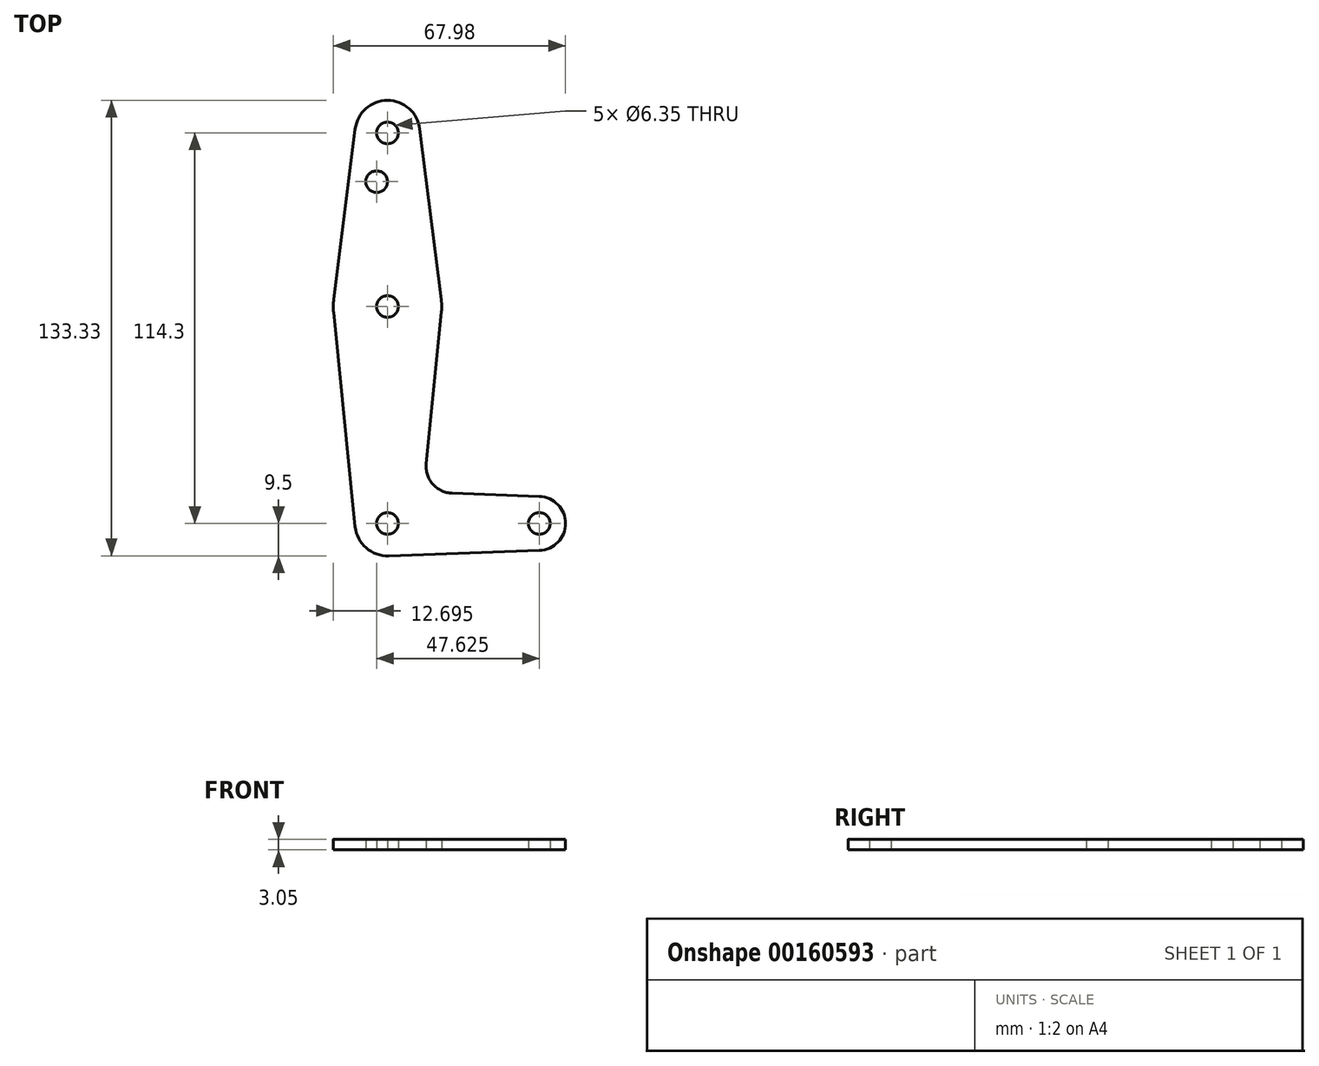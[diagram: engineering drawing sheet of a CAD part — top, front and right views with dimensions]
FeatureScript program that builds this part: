
annotation { "Feature Type Name" : "Feature", "Feature Type Description" : "" }
export const myFeature = defineFeature(function(context is Context, id is Id, definition is map)
    precondition{}
    {
        {
            var Q0;
            Q0=qCreatedBy(makeId("Top.planeOp"),FACE);
            var sketch = newSketch(context, id + "F0", { "sketchPlane" : qUnion([Q0])});
            skLineSegment(sketch, "E0", {"start": v(0, 0) * mm, "end": v(44.45, 0) * mm, "construction": true});
            skLineSegment(sketch, "E1", {"start": v(0, 0) * mm, "end": v(0, 114.3) * mm, "construction": true});
            skCircle(sketch, "E2", {"center": v(0, 0) * mm, "radius": 9.5 * mm});
            skCircle(sketch, "E3", {"center": v(44.17, 0) * mm, "radius": 7.94 * mm});
            skCircle(sketch, "E4", {"center": v(0, 114.3) * mm, "radius": 9.53 * mm});
            skCircle(sketch, "E5", {"center": v(0, 63.5) * mm, "radius": 15.88 * mm});
            skLineSegment(sketch, "E6", {"start": v(9.45, 115.5) * mm, "end": v(15.75, 65.48) * mm});
            skLineSegment(sketch, "E7", {"start": v(-9.45, 115.5) * mm, "end": v(-15.75, 65.48) * mm});
            skLineSegment(sketch, "E8", {"start": v(-15.8, 61.9) * mm, "end": v(-9.45, -0.95) * mm});
            skLineSegment(sketch, "E9", {"start": v(15.8, 61.9) * mm, "end": v(11.32, 17.58) * mm});
            skLineSegment(sketch, "E10", {"start": v(18.95, 8.83) * mm, "end": v(44.45, 7.93) * mm});
            skLineSegment(sketch, "E11", {"start": v(0.34, -9.5) * mm, "end": v(44.45, -7.93) * mm});
            skCircle(sketch, "E12", {"center": v(0, 114.3) * mm, "radius": 3.18 * mm});
            skCircle(sketch, "E13", {"center": v(0, 63.5) * mm, "radius": 3.18 * mm});
            skCircle(sketch, "E14", {"center": v(0, 0) * mm, "radius": 3.18 * mm});
            skCircle(sketch, "E15", {"center": v(44.45, 0) * mm, "radius": 3.18 * mm});
            skCircle(sketch, "E16", {"center": v(-3.17, 100.03) * mm, "radius": 3.18 * mm});
            skPoint(sketch, "E17.newPointA", {"position": v(9.45, -0.95) * mm});
            skArc(sketch, "E17.filletArc", {"start": v(11.32, 17.58) * mm, "mid": v(13.24, 11.55) * mm, "end": v(18.95, 8.83) * mm});
            skSolve(sketch);
        }
        {
            var Q0;
            Q0 = qSketchRegion(id + "F0", true);
            extrude(context, id + "F1", {"entities" : qUnion([Q0]), "depth" : 3.05 * mm});
        }
    });
